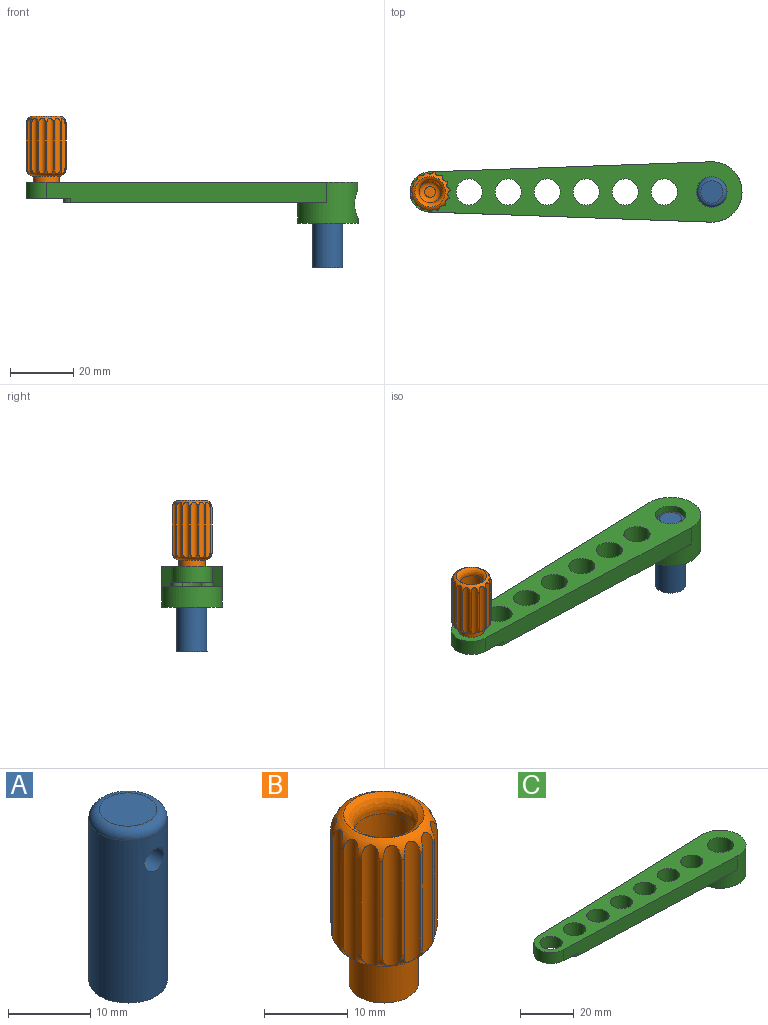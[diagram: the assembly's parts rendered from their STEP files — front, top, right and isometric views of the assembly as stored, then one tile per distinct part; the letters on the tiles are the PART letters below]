
ASSEMBLY  parts=3 mates=1
PART A: 5 faces, bbox 10.3x10.3x25.4 mm
  f0: cylinder r=4.76mm len=24.13mm, axis (0,0,1), area 704.7mm2, adj f1,f3,f4
  f1: plane 9.53x9.53mm, normal (0,0,-1), area 71.3mm2, adj f0
  f2: plane 6.99x6.99mm, normal (0,0,1), area 38.3mm2, adj f4
  f3: cylinder r=1.65mm len=9.53mm, axis (0,-1,0), area 95.8mm2, adj f0
  f4: torus R=3.49mm, axis (0,0,1), area 53.9mm2, adj f0,f2
PART B: 40 faces, bbox 13.7x13.7x24.8 mm
  f0: cylinder r=6.35mm len=13.99mm, axis (0,0,-1), area 6.3mm2, adj f17,f18,f32,f33
  f1: cylinder r=6.35mm len=13.99mm, axis (0,0,-1), area 6.3mm2, adj f17,f18,f30,f32
  f2: cylinder r=6.35mm len=13.99mm, axis (0,0,-1), area 6.3mm2, adj f17,f18,f19,f31
  f3: cylinder r=6.35mm len=13.99mm, axis (0,0,-1), area 6.3mm2, adj f17,f18,f30,f31
  f4: cylinder r=6.35mm len=13.99mm, axis (0,0,-1), area 6.3mm2, adj f17,f18,f28,f29
  f5: cylinder r=6.35mm len=13.99mm, axis (0,0,-1), area 6.3mm2, adj f17,f18,f28,f33
  f6: cylinder r=6.35mm len=13.99mm, axis (0,0,-1), area 6.3mm2, adj f17,f18,f27,f29
  f7: cylinder r=6.35mm len=13.99mm, axis (0,0,-1), area 6.3mm2, adj f17,f18,f26,f27
  f8: cylinder r=6.35mm len=13.99mm, axis (0,0,-1), area 6.3mm2, adj f17,f18,f23,f25
  f9: cylinder r=6.35mm len=13.99mm, axis (0,0,-1), area 6.3mm2, adj f17,f18,f24,f25
  f10: cylinder r=6.35mm len=13.99mm, axis (0,0,-1), area 6.3mm2, adj f17,f18,f22,f23
  f11: cylinder r=6.35mm len=13.99mm, axis (0,0,-1), area 6.3mm2, adj f17,f18,f20,f22
  f12: cylinder r=6.35mm len=13.99mm, axis (0,0,-1), area 6.3mm2, adj f17,f18,f21,f26
  f13: cylinder r=6.35mm len=13.99mm, axis (0,0,-1), area 6.3mm2, adj f17,f18,f20,f21
  f14: cylinder r=4.13mm len=8.26mm, axis (0,0,-1), area 148.2mm2, adj f15,f17
  f15: plane 8.26x8.26mm, normal (0,0,-1), area 48.5mm2, adj f14,f34
  f16: cylinder r=6.35mm len=13.99mm, axis (0,0,-1), area 6.3mm2, adj f17,f18,f19,f24
  f17: torus R=3.81mm, axis (0,0,-1), area 75.5mm2, adj f0,f1,f2,f3,f4,f5,f6,f7
  f18: torus R=3.81mm, axis (0,0,1), area 56mm2, adj f0,f1,f2,f3,f4,f5,f6,f7
  f19: cylinder r=1.27mm len=17.55mm, axis (0,0,1), area 44.5mm2, adj f2,f16,f17,f18
  f20: cylinder r=1.27mm len=17.55mm, axis (0,0,1), area 44.5mm2, adj f11,f13,f17,f18
  f21: cylinder r=1.27mm len=17.55mm, axis (0,0,1), area 44.5mm2, adj f12,f13,f17,f18
  f22: cylinder r=1.27mm len=17.55mm, axis (0,0,1), area 44.5mm2, adj f10,f11,f17,f18
  f23: cylinder r=1.27mm len=17.55mm, axis (0,0,1), area 44.5mm2, adj f8,f10,f17,f18
  f24: cylinder r=1.27mm len=17.55mm, axis (0,0,1), area 44.5mm2, adj f9,f16,f17,f18
  f25: cylinder r=1.27mm len=17.55mm, axis (0,0,1), area 44.5mm2, adj f8,f9,f17,f18
  f26: cylinder r=1.27mm len=17.55mm, axis (0,0,1), area 44.5mm2, adj f7,f12,f17,f18
  f27: cylinder r=1.27mm len=17.55mm, axis (0,0,1), area 44.5mm2, adj f6,f7,f17,f18
  f28: cylinder r=1.27mm len=17.55mm, axis (0,0,1), area 44.5mm2, adj f4,f5,f17,f18
  f29: cylinder r=1.27mm len=17.55mm, axis (0,0,1), area 44.5mm2, adj f4,f6,f17,f18
  f30: cylinder r=1.27mm len=17.55mm, axis (0,0,1), area 44.5mm2, adj f1,f3,f17,f18
  f31: cylinder r=1.27mm len=17.55mm, axis (0,0,1), area 44.5mm2, adj f2,f3,f17,f18
  f32: cylinder r=1.27mm len=17.55mm, axis (0,0,1), area 44.5mm2, adj f0,f1,f17,f18
  f33: cylinder r=1.27mm len=17.55mm, axis (0,0,1), area 44.5mm2, adj f0,f5,f17,f18
  f34: cylinder r=1.27mm len=8.89mm, axis (0,0,-1), area 70.9mm2, adj f15,f35
  f35: plane 2.54x2.54mm, normal (0,0,-1), area 5.1mm2, adj f34
  f36: cylinder r=3.49mm len=6.99mm, axis (0,0,1), area 128.2mm2, adj f38,f39
  f37: plane 3.43x3.43mm, normal (0,0,1), area 9.2mm2, adj f39
  f38: bspline ~12.38x12.38mm, area 70.2mm2, adj f18,f36
  f39: torus R=1.71mm, axis (0,0,1), area 49.9mm2, adj f36,f37
PART C: 24 faces, bbox 104.8x19.1x13 mm
  f0: cylinder r=1.59mm len=3.18mm, axis (1,0,0), area 29.2mm2, adj f3,f21
  f1: cylinder r=4.13mm len=8.26mm, axis (0,0,1), area 131.7mm2, adj f5,f19
  f2: cylinder r=1.59mm len=3.18mm, axis (1,0,0), area 16.5mm2, adj f3,f17
  f3: cylinder r=4.83mm len=12.95mm, axis (0,0,-1), area 376.7mm2, adj f0,f2,f5,f6
  f4: cylinder r=9.53mm len=19.05mm, axis (0,0,-1), area 525.7mm2, adj f5,f6,f8,f15,f16,f20
  f5: plane 104.78x19.05mm, normal (0,0,1), area 1170mm2, adj f1,f3,f4,f7,f8,f9,f10,f11
  f6: plane 19.05x19.05mm, normal (0,0,-1), area 211.9mm2, adj f3,f4
  f7: cylinder r=4.13mm len=8.26mm, axis (0,0,1), area 164.7mm2, adj f5,f16
  f8: plane 88.56x6.35mm, normal (-0.04,-1,0), area 552.8mm2, adj f4,f5,f14,f16,f19,f23
  f9: cylinder r=4.13mm len=8.26mm, axis (0,0,1), area 164.7mm2, adj f5,f16
  f10: cylinder r=4.13mm len=8.26mm, axis (0,0,1), area 164.7mm2, adj f5,f16
  f11: cylinder r=4.13mm len=8.26mm, axis (0,0,1), area 164.7mm2, adj f5,f16
  f12: cylinder r=4.13mm len=8.26mm, axis (0,0,1), area 164.7mm2, adj f5,f16
  f13: cylinder r=4.13mm len=8.26mm, axis (0,0,1), area 164.7mm2, adj f5,f16
  f14: cylinder r=6.35mm len=12.7mm, axis (0,0,1), area 101mm2, adj f5,f8,f15,f19
  f15: plane 88.63x6.35mm, normal (-0.04,1,0), area 553.1mm2, adj f4,f5,f14,f16,f19,f22
  f16: plane 83.21x19.04mm, normal (0,0,-1), area 872mm2, adj f4,f7,f8,f9,f10,f11,f12,f13
  f17: plane 3.18x3.18mm, normal (1,0,0), area 7.9mm2, adj f2
  f18: cylinder r=6.35mm len=5.85mm, axis (0,0,-1), area 7.7mm2, adj f16,f19,f22,f23
  f19: plane 14.15x13.26mm, normal (0,0,-1), area 86.1mm2, adj f1,f8,f14,f15,f18,f22,f23
  f20: cylinder r=4.45mm len=8.89mm, axis (1,0,0), area 38mm2, adj f4,f21
  f21: plane 8.89x8.89mm, normal (1,0,0), area 54.2mm2, adj f0,f20
  f22: cylinder r=2.54mm len=3.71mm, axis (0,0,-1), area 6.5mm2, adj f15,f16,f18,f19
  f23: cylinder r=2.54mm len=3.71mm, axis (0,0,-1), area 6.5mm2, adj f8,f16,f18,f19
PLACE A rot(axis=(0,0,1),90deg) t=(1.31,-3.99,0.25)mm
PLACE B t=(-87.59,-3.99,-2.03)mm
PLACE C t=(1.31,-3.99,-11.18)mm
MATE fastened A.f0 <-> C.f3  axis (0,0,1) through (1.31,-3.99,0.25)mm
